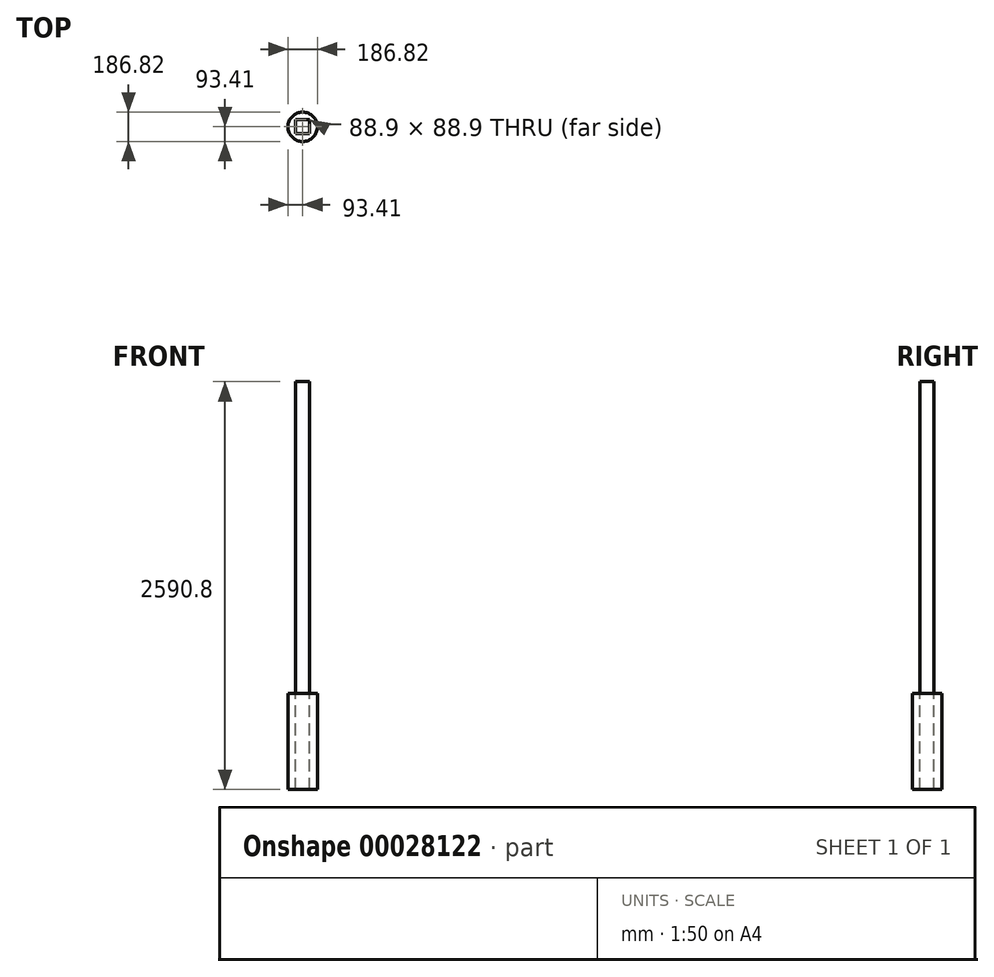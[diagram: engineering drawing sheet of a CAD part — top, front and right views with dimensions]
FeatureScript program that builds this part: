
annotation { "Feature Type Name" : "Feature", "Feature Type Description" : "" }
export const myFeature = defineFeature(function(context is Context, id is Id, definition is map)
    precondition{}
    {
        {
            var Q0;
            Q0=qCreatedBy(makeId("Top.planeOp"),FACE);
            var sketch = newSketch(context, id + "F0", { "sketchPlane" : qUnion([Q0])});
            skLineSegment(sketch, "E0.bottom", {"start": v(0, 0) * mm, "end": v(88.9, 0) * mm});
            skLineSegment(sketch, "E0.top", {"start": v(0, 88.9) * mm, "end": v(88.9, 88.9) * mm});
            skLineSegment(sketch, "E0.left", {"start": v(0, 0) * mm, "end": v(0, 88.9) * mm});
            skLineSegment(sketch, "E0.right", {"start": v(88.9, 0) * mm, "end": v(88.9, 88.9) * mm});
            skCircle(sketch, "E1", {"center": v(44.45, 44.45) * mm, "radius": 93.4 * mm});
            skLineSegment(sketch, "E2", {"start": v(0, 88.9) * mm, "end": v(88.9, 0) * mm, "construction": true});
            skSolve(sketch);
        }
        {
            var Q0;
            Q0=makeQuery(id+"F0.imprint","IMPRINT",FACE,{"disambiguationData":[TD([[makeQuery(id+"F0.imprint","IMPRINT",EDGE,{"derivedFrom":sQuery(id+"F0.wireOp",EDGE,"E0.bottom")}),1.0]])]});
            extrude(context, id + "F1", {"entities" : qUnion([Q0]), "depth" : 1981.2 * mm});
        }
        {
            var Q0;
            Q0=makeQuery(id+"F0.imprint","IMPRINT",FACE,{"disambiguationData":[TD([[makeQuery(id+"F0.imprint","IMPRINT",EDGE,{"derivedFrom":sQuery(id+"F0.wireOp",EDGE,"E0.bottom")}),-1.0]])]});
            extrude(context, id + "F2", {"entities" : qUnion([Q0]), "operationType" : NewBodyOperationType.ADD, "oppositeDirection" : true, "depth" : 609.6 * mm});
        }
        {
            var Q0;
            Q0=qCreatedBy(makeId("Right.planeOp"),FACE);
            var sketch = newSketch(context, id + "F3", { "sketchPlane" : qUnion([Q0])});
            skLineSegment(sketch, "E3.bottom", {"start": v(0, 0) * mm, "end": v(-88.9, 0) * mm});
            skLineSegment(sketch, "E3.top", {"start": v(0, 38.1) * mm, "end": v(-88.9, 38.1) * mm});
            skLineSegment(sketch, "E3.left", {"start": v(0, 0) * mm, "end": v(0, 38.1) * mm});
            skLineSegment(sketch, "E3.right", {"start": v(-88.9, 0) * mm, "end": v(-88.9, 38.1) * mm});
            skSolve(sketch);
        }
        {
            var Q0;
            Q0=makeQuery(id+"F3.imprint","IMPRINT",FACE,{"disambiguationData":[TD([[makeQuery(id+"F3.imprint","IMPRINT",EDGE,{"derivedFrom":sQuery(id+"F3.wireOp",EDGE,"E3.bottom")}),-1.0]])]});
            extrude(context, id + "F4", {"entities" : qUnion([Q0]), "oppositeDirection" : true, "depth" : 1828.8 * mm});
        }
        {
            var Q0;
            Q0=makeQuery(id+"F4.opExtrude","SWEPT_BODY",BODY,{"disambiguationData":[OSD([sQuery(id+"F3.wireOp",EDGE,"E3.bottom"),sQuery(id+"F3.wireOp",EDGE,"E3.top"),sQuery(id+"F3.wireOp",EDGE,"E3.left"),sQuery(id+"F3.wireOp",EDGE,"E3.right")])]});
            deleteBodies(context, id + "F5", {"entities" : qUnion([Q0])});
        }
    });
